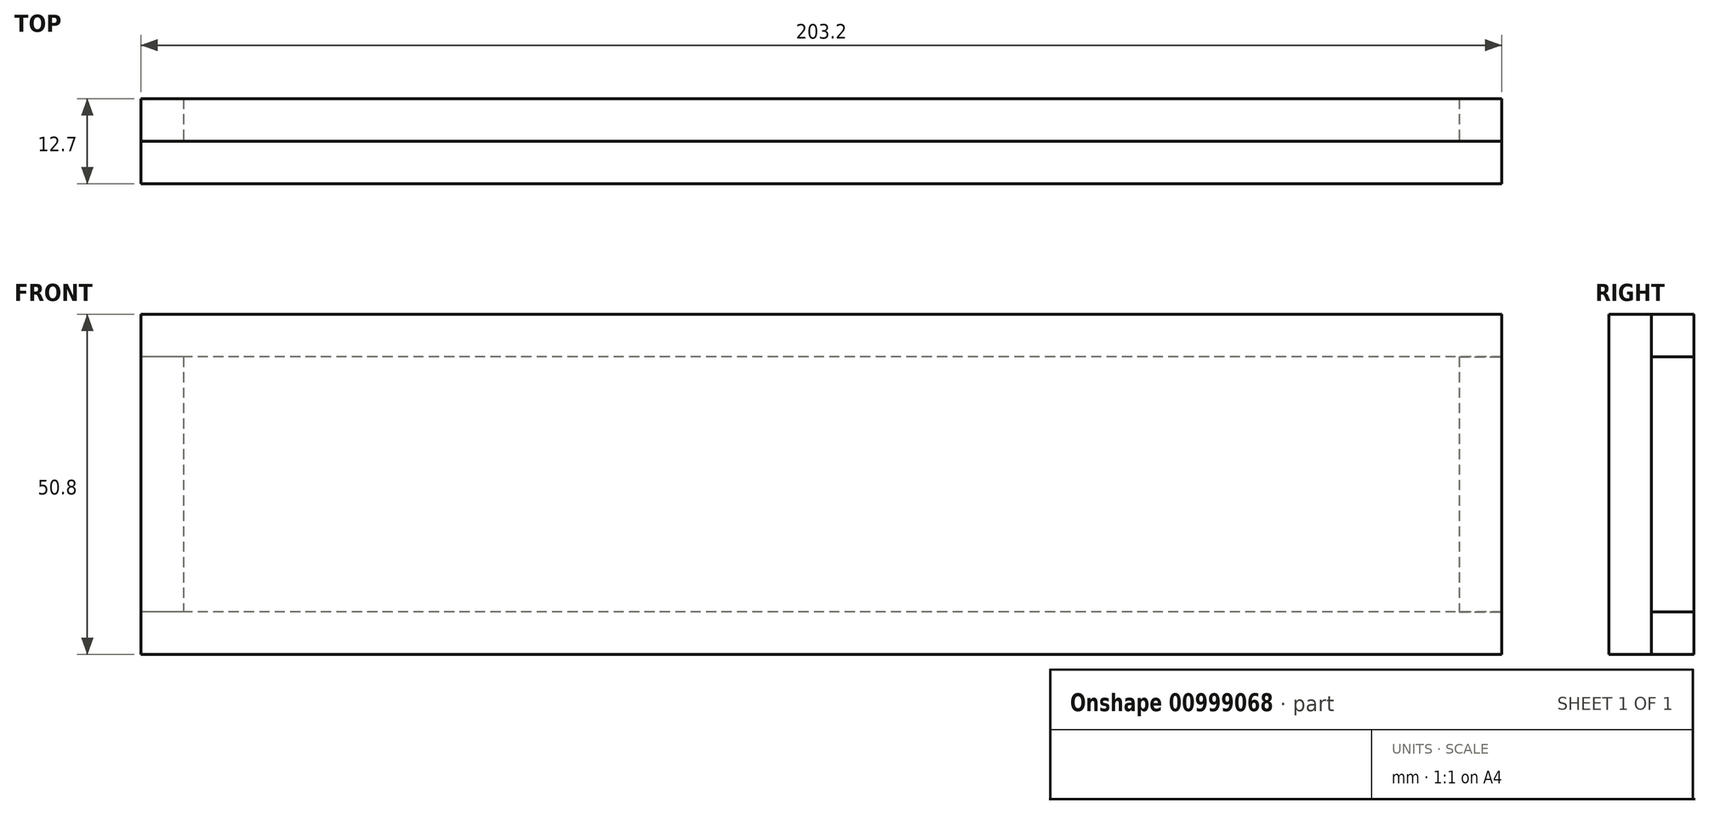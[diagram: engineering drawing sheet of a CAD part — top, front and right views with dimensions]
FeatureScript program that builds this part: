
annotation { "Feature Type Name" : "Feature", "Feature Type Description" : "" }
export const myFeature = defineFeature(function(context is Context, id is Id, definition is map)
    precondition{}
    {
        {
            var Q0;
            Q0=qCreatedBy(makeId("Front.planeOp"),FACE);
            var sketch = newSketch(context, id + "F0", { "sketchPlane" : qUnion([Q0])});
            skLineSegment(sketch, "E0.bottom", {"start": v(101.6, 25.4) * mm, "end": v(-101.6, 25.4) * mm});
            skLineSegment(sketch, "E0.top", {"start": v(101.6, -25.4) * mm, "end": v(-101.6, -25.4) * mm});
            skLineSegment(sketch, "E0.left", {"start": v(101.6, 25.4) * mm, "end": v(101.6, -25.4) * mm});
            skLineSegment(sketch, "E0.right", {"start": v(-101.6, 25.4) * mm, "end": v(-101.6, -25.4) * mm});
            skPoint(sketch, "E0.middle", {"position": v(0, 0) * mm});
            skSolve(sketch);
        }
        {
            var Q0;
            Q0=makeQuery(id+"F0.imprint","IMPRINT",FACE,{"disambiguationData":[TD([[makeQuery(id+"F0.imprint","IMPRINT",EDGE,{"derivedFrom":sQuery(id+"F0.wireOp",EDGE,"E0.bottom")}),1.0]])]});
            extrude(context, id + "F1", {"entities" : qUnion([Q0]), "endBound" : BoundingType.SYMMETRIC, "depth" : 6.35 * mm, "offsetDistance" : 25.4 * mm});
        }
        {
            var Q0;
            Q0=makeQuery(id+"F1.opExtrude","CAP_FACE",FACE,{"disambiguationData":[OSD([sQuery(id+"F0.wireOp",EDGE,"E0.bottom"),sQuery(id+"F0.wireOp",EDGE,"E0.top"),sQuery(id+"F0.wireOp",EDGE,"E0.left"),sQuery(id+"F0.wireOp",EDGE,"E0.right")])],"isStart":true});
            var sketch = newSketch(context, id + "F2", { "sketchPlane" : qUnion([Q0])});
            skLineSegment(sketch, "E1.bottom", {"start": v(-101.6, 25.4) * mm, "end": v(101.6, 25.4) * mm});
            skLineSegment(sketch, "E1.top", {"start": v(-101.6, 19.05) * mm, "end": v(101.6, 19.05) * mm});
            skLineSegment(sketch, "E1.left", {"start": v(-101.6, 25.4) * mm, "end": v(-101.6, 19.05) * mm});
            skLineSegment(sketch, "E1.right", {"start": v(101.6, 25.4) * mm, "end": v(101.6, 19.05) * mm});
            skSolve(sketch);
        }
        {
            var Q0;
            Q0=makeQuery(id+"F2.imprint","IMPRINT",FACE,{"disambiguationData":[TD([[makeQuery(id+"F2.imprint","IMPRINT",EDGE,{"derivedFrom":sQuery(id+"F2.wireOp",EDGE,"E1.bottom")}),-1.0]])]});
            extrude(context, id + "F3", {"entities" : qUnion([Q0]), "depth" : 6.35 * mm, "offsetDistance" : 25.4 * mm});
        }
        {
            var Q0;
            Q0=makeQuery(id+"F3.opExtrude","SWEPT_BODY",BODY,{"disambiguationData":[OSD([sQuery(id+"F2.wireOp",EDGE,"E1.bottom"),sQuery(id+"F2.wireOp",EDGE,"E1.top"),sQuery(id+"F2.wireOp",EDGE,"E1.left"),sQuery(id+"F2.wireOp",EDGE,"E1.right")])]});
            var Q1;
            Q1=qCreatedBy(makeId("Top.planeOp"),FACE);
            mirror(context, id + "F4", {"entities" : qUnion([Q0]), "mirrorPlane" : qUnion([Q1])});
        }
        {
            var Q0;
            Q0=makeQuery(id+"F1.opExtrude","CAP_FACE",FACE,{"disambiguationData":[OSD([sQuery(id+"F0.wireOp",EDGE,"E0.bottom"),sQuery(id+"F0.wireOp",EDGE,"E0.top"),sQuery(id+"F0.wireOp",EDGE,"E0.left"),sQuery(id+"F0.wireOp",EDGE,"E0.right")])],"isStart":true});
            var sketch = newSketch(context, id + "F5", { "sketchPlane" : qUnion([Q0])});
            skLineSegment(sketch, "E2.0", {"start": v(95.25, 19.05) * mm, "end": v(101.6, 19.05) * mm});
            skLineSegment(sketch, "E3.0", {"start": v(101.6, 25.4) * mm, "end": v(101.6, -25.4) * mm});
            skLineSegment(sketch, "E4.0", {"start": v(-101.6, -19.05) * mm, "end": v(101.6, -19.05) * mm});
            skLineSegment(sketch, "E5.bottom", {"start": v(101.6, 19.05) * mm, "end": v(95.25, 19.05) * mm});
            skLineSegment(sketch, "E5.top", {"start": v(101.6, -19.05) * mm, "end": v(95.25, -19.05) * mm});
            skLineSegment(sketch, "E5.left", {"start": v(101.6, 19.05) * mm, "end": v(101.6, -19.05) * mm});
            skLineSegment(sketch, "E5.right", {"start": v(95.25, 19.05) * mm, "end": v(95.25, -19.05) * mm});
            skPoint(sketch, "E6.orphan", {"position": v(-101.6, 19.05) * mm});
            skSolve(sketch);
        }
        {
            var Q0;
            {var subQ0=sQuery(id+"F5.wireOp",EDGE,"E2.0");Q0=makeQuery(id+"F5.imprint","IMPRINT",FACE,{"disambiguationData":[TD([[makeQuery(id+"F5.imprint","IMPRINT",EDGE,{"derivedFrom":subQ0}),-1.0]])]});}
            extrude(context, id + "F6", {"entities" : qUnion([Q0]), "depth" : 6.35 * mm, "offsetDistance" : 25.4 * mm});
        }
        {
            var Q0;
            Q0=makeQuery(id+"F6.opExtrude","SWEPT_BODY",BODY,{"disambiguationData":[OSD([sQuery(id+"F5.wireOp",EDGE,"E2.0"),sQuery(id+"F5.wireOp",EDGE,"E3.0"),sQuery(id+"F5.wireOp",EDGE,"E4.0"),sQuery(id+"F5.wireOp",EDGE,"E5.right")])]});
            var Q1;
            Q1=qCreatedBy(makeId("Right.planeOp"),FACE);
            mirror(context, id + "F7", {"entities" : qUnion([Q0]), "mirrorPlane" : qUnion([Q1])});
        }
    });
